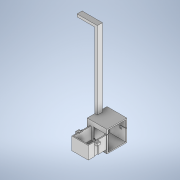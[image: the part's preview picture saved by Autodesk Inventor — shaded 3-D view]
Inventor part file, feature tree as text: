
AUTODESK INVENTOR PART (.ipt)
format: ipt  version: 2020.2 (Build 242310000, 310)  size: 564,224 bytes
history: native  units: mm
features: sketch x25, extrude x24, projected_geometry x8, hole x1
ambient origin geometry x8: Origin, YZ Plane, XZ Plane, XY Plane, X Axis, Y Axis, Z Axis, Center Point
bodies: Solid1 (feature_tree)
feature tree (58):
  sketch  "Sketch1"  dims[d0=29.0mm d1=35.0mm]
  extrude  "Extrusion1"  Depth=35.0mm
  extrude  "Extrusion2"  Depth=2.0mm
  extrude  "Extrusion3"  Depth=39.0mm
  hole  "Hole1"  [1 undecoded]
  extrude  "Extrusion4"  Depth=10.0mm
  sketch  "Sketch5"  dims[d10=10.0mm d11=0.0mm d12=4.2mm]
  sketch  "Sketch6"  dims[d13=4.475mm d14=26.05mm]
  extrude  "Extrusion5"  Depth=26.05mm
  extrude  "Extrusion6"  Depth=39.0mm
  extrude  "Extrusion7"  Depth=33.0mm TaperAngle=0.0deg
  sketch  "Sketch10"  dims[d27=7.0mm d28=7.0mm]
  extrude  "Extrusion8"  Depth=7.0mm
  extrude  "Extrusion9"  Depth=7.0mm
  extrude  "Extrusion14"  Depth=10.0mm
  extrude  "Extrusion15"  Depth=20.0mm
  extrude  "Extrusion16"  Depth=22.5mm
  extrude  "Extrusion17"  Depth=1.0mm
  extrude  "Extrusion18"  Depth=24.0mm
  extrude  "Extrusion19"  Depth=1.0mm
  extrude  "Extrusion25"  Depth=26.0mm
  extrude  "Extrusion26"  Depth=1.0mm
  extrude  "Extrusion27"  Depth=1.0mm
  extrude  "Extrusion21"  Depth=26.0mm TaperAngle=0.0deg
  extrude  "Extrusion22"  Depth=1.0mm TaperAngle=0.0deg
  extrude  "Extrusion23"  Depth=14.0mm
  extrude  "Extrusion24"  TaperAngle=90.0deg  [1 undecoded]
  extrude  "Extrusion28"  Depth=3.5mm
  extrude  "Extrusion29"  Depth=7.0mm
  sketch  "Sketch2"  dims[d2=2.0mm d3=2.0mm]
  sketch  "Sketch3"  dims[d4=33.0mm d5=39.0mm]
  sketch  "Sketch4"  dims[d6=2.0mm d7=0.0mm d8=40.0mm d9=0.0mm]
  sketch  "Sketch7"  dims[d15=29.6mm]
  projected_geometry  "Projected Loop1"
  sketch  "Sketch8"  dims[d16=3.4mm d17=6.0mm d18=6.3mm d19=2.0mm d20=90.0deg d21=8.0mm d22=20.594885mm d23=39.0mm]
  sketch  "Sketch9"  dims[d24=2.0mm d25=33.0mm d26=0.0mm]
  sketch  "Sketch11"  dims[d29=7.0mm d30=7.0mm]
  sketch  "Sketch16"  dims[d31=5.0mm d32=0.0mm d33=10.0mm]
  sketch  "Sketch17"  dims[d34=3.5mm d35=20.0mm]
  sketch  "Sketch18"  dims[d36=90.0deg d37=22.5mm]
  projected_geometry  "Projected Loop4"
  sketch  "Sketch19"  dims[d38=10.0mm d39=0.0mm d40=1.0mm]
  projected_geometry  "Projected Loop5"
  sketch  "Sketch21"  dims[d41=10.0mm d42=0.0mm d43=24.0mm]
  projected_geometry  "Projected Loop6"
  sketch  "Sketch25"  dims[d44=30.48mm d45=1.0mm]
  sketch  "Sketch26"  dims[d46=31.48mm d47=26.0mm]
  sketch  "Sketch27"  dims[d48=34.0mm d49=0.0mm d50=1.0mm]
  sketch  "Sketch28"  dims[d51=29.48mm d52=0.0mm d69=1.0mm]
  sketch  "Sketch30"  dims[d70=35.0mm d71=26.0mm d72=0.0mm]
  projected_geometry  "Projected Loop7"
  sketch  "Sketch31"  dims[d73=10.0mm d74=0.0mm d75=1.0mm d76=0.0mm]
  projected_geometry  "Projected Loop8"
  sketch  "Sketch32"  dims[d77=1.0mm d78=0.0mm d79=14.0mm]
  projected_geometry  "Projected Loop9"
  projected_geometry  "Projected Loop10"
  sketch  "Sketch34"  dims[d80=17.5mm d81=90.0deg]
  sketch  "Sketch35"  dims[d82=35.0mm d83=3.5mm d84=7.0mm d85=7.0mm d86=7.0mm d87=3.4mm d88=3.4mm d89=5.0mm d90=0.0mm d91=1.0mm d92=0.0mm d118=15.0mm d119=10.0mm d120=5.0mm d121=12.7mm d122=0.0mm d123=5.0mm d124=35.0mm d125=0.0mm d126=152.6502mm d127=0.0mm d128=5.0mm d129=35.0mm d130=0.0mm d131=1.0mm d132=0.0mm d133=1.0mm d134=0.0mm d135=1.0mm d136=0.0mm d137=1.0mm d138=0.0mm d139=16.0mm d140=10.0mm d141=1.5mm d142=2.0mm d143=5.0mm d144=3.5mm d145=5.5mm d146=10.0mm d147=0.0mm d54=0.5mm d55=0.872665mm d56=0.5mm d57=0.872665mm d58=0.5mm d59=0.872665mm d60=0.5mm d61=0.872665mm d116=0.5mm d117=0.872665mm]
note: 2 required parameter values undecoded (feature->parameter linkage not recoverable at this tier; creation-order binding heuristic only, values carry confidence <= 0.55)
